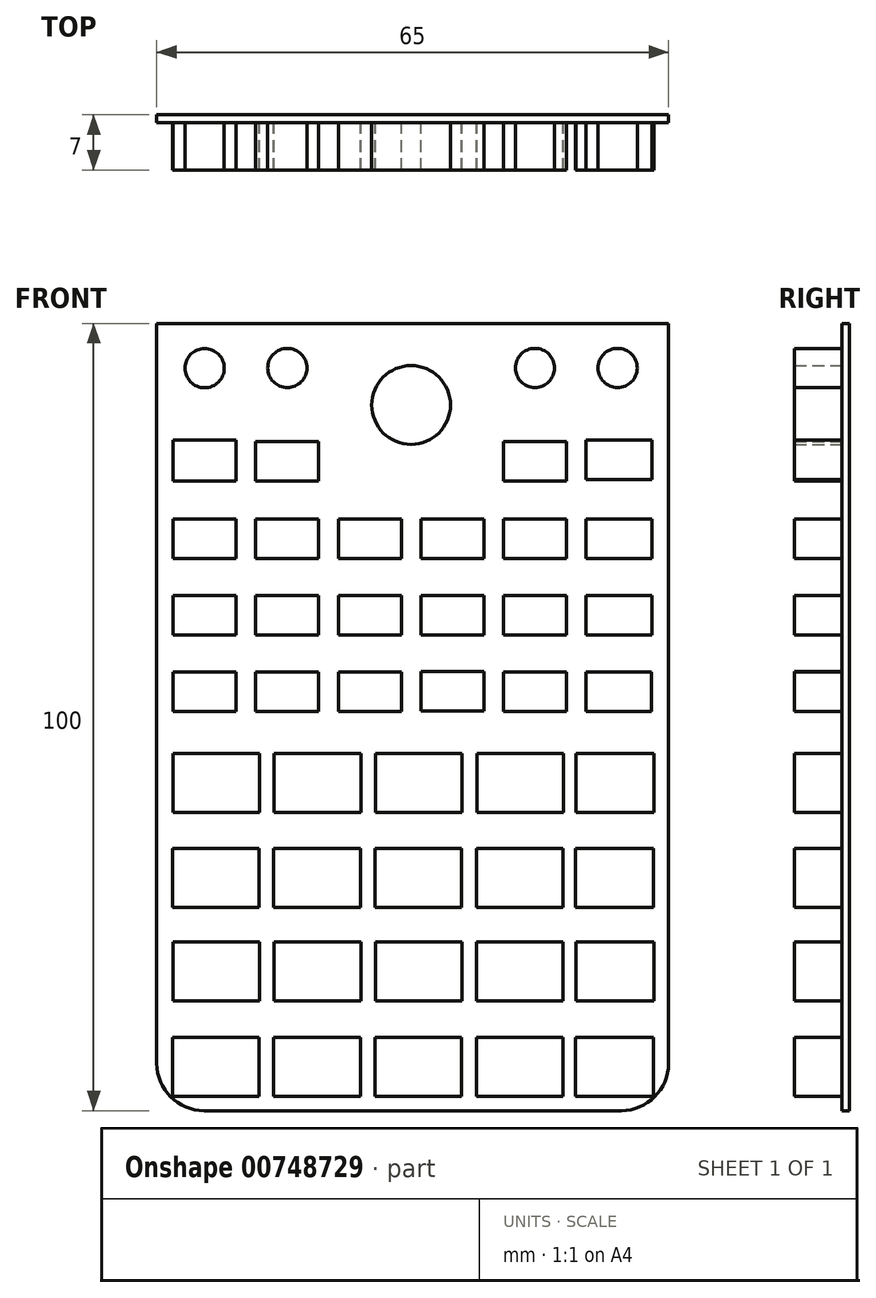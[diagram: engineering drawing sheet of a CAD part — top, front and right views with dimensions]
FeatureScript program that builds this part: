
annotation { "Feature Type Name" : "Feature", "Feature Type Description" : "" }
export const myFeature = defineFeature(function(context is Context, id is Id, definition is map)
    precondition{}
    {
        {
            var Q0;
            Q0=qCreatedBy(makeId("Front.planeOp"),FACE);
            var sketch = newSketch(context, id + "F0", { "sketchPlane" : qUnion([Q0])});
            skLineSegment(sketch, "E0.bottom", {"start": v(-31.37, 29.86) * mm, "end": v(33.63, 29.86) * mm});
            skLineSegment(sketch, "E0.top", {"start": v(-25.38, -70.14) * mm, "end": v(27.63, -70.14) * mm});
            skLineSegment(sketch, "E0.left", {"start": v(-31.37, 29.86) * mm, "end": v(-31.37, -64.14) * mm});
            skLineSegment(sketch, "E0.right", {"start": v(33.63, 29.86) * mm, "end": v(33.63, -64.14) * mm});
            skPoint(sketch, "E1.visualSharp", {"position": v(33.63, -70.14) * mm});
            skArc(sketch, "E1.filletArc", {"start": v(27.63, -70.14) * mm, "mid": v(31.87, -68.38) * mm, "end": v(33.63, -64.14) * mm});
            skPoint(sketch, "E2.visualSharp", {"position": v(-31.37, -70.14) * mm});
            skArc(sketch, "E2.filletArc", {"start": v(-31.37, -64.14) * mm, "mid": v(-29.62, -68.38) * mm, "end": v(-25.38, -70.14) * mm});
            skLineSegment(sketch, "E3", {"start": v(-29.36, -68.3) * mm, "end": v(-18.36, -68.3) * mm});
            skLineSegment(sketch, "E4", {"start": v(-18.36, -68.3) * mm, "end": v(-18.36, -60.81) * mm});
            skLineSegment(sketch, "E5", {"start": v(-18.36, -60.81) * mm, "end": v(-29.36, -60.81) * mm});
            skLineSegment(sketch, "E6", {"start": v(-29.36, -60.81) * mm, "end": v(-29.36, -68.3) * mm});
            skLineSegment(sketch, "E7", {"start": v(-29.36, -68.3) * mm, "end": v(-23.86, -68.3) * mm});
            skLineSegment(sketch, "E8", {"start": v(-16.51, -68.3) * mm, "end": v(-5.52, -68.3) * mm});
            skLineSegment(sketch, "E9", {"start": v(-5.52, -68.3) * mm, "end": v(-5.52, -60.81) * mm});
            skLineSegment(sketch, "E10", {"start": v(-5.52, -60.81) * mm, "end": v(-16.51, -60.81) * mm});
            skLineSegment(sketch, "E11", {"start": v(-16.51, -60.81) * mm, "end": v(-16.51, -68.3) * mm});
            skLineSegment(sketch, "E12", {"start": v(-16.51, -68.3) * mm, "end": v(-11.01, -68.3) * mm});
            skLineSegment(sketch, "E13", {"start": v(-3.66, -68.3) * mm, "end": v(7.34, -68.3) * mm});
            skLineSegment(sketch, "E14", {"start": v(7.34, -68.3) * mm, "end": v(7.34, -60.81) * mm});
            skLineSegment(sketch, "E15", {"start": v(7.34, -60.81) * mm, "end": v(-3.66, -60.81) * mm});
            skLineSegment(sketch, "E16", {"start": v(-3.66, -60.81) * mm, "end": v(-3.66, -68.3) * mm});
            skLineSegment(sketch, "E17", {"start": v(-3.66, -68.3) * mm, "end": v(1.84, -68.3) * mm});
            skLineSegment(sketch, "E18", {"start": v(9.22, -68.3) * mm, "end": v(20.22, -68.3) * mm});
            skLineSegment(sketch, "E19", {"start": v(20.22, -68.3) * mm, "end": v(20.22, -60.81) * mm});
            skLineSegment(sketch, "E20", {"start": v(20.22, -60.81) * mm, "end": v(9.22, -60.81) * mm});
            skLineSegment(sketch, "E21", {"start": v(9.22, -60.81) * mm, "end": v(9.22, -68.3) * mm});
            skLineSegment(sketch, "E22", {"start": v(9.22, -68.3) * mm, "end": v(14.72, -68.3) * mm});
            skLineSegment(sketch, "E23", {"start": v(21.82, -68.3) * mm, "end": v(31.72, -68.3) * mm});
            skLineSegment(sketch, "E24", {"start": v(31.72, -68.3) * mm, "end": v(31.72, -60.81) * mm});
            skLineSegment(sketch, "E25", {"start": v(31.72, -60.81) * mm, "end": v(21.82, -60.81) * mm});
            skLineSegment(sketch, "E26", {"start": v(21.82, -60.81) * mm, "end": v(21.82, -68.3) * mm});
            skLineSegment(sketch, "E27", {"start": v(21.82, -68.3) * mm, "end": v(26.49, -68.3) * mm});
            skLineSegment(sketch, "E28", {"start": v(-29.3, -56.22) * mm, "end": v(-18.3, -56.22) * mm});
            skLineSegment(sketch, "E29", {"start": v(-18.3, -56.22) * mm, "end": v(-18.3, -48.73) * mm});
            skLineSegment(sketch, "E30", {"start": v(-18.3, -48.73) * mm, "end": v(-29.3, -48.73) * mm});
            skLineSegment(sketch, "E31", {"start": v(-29.3, -48.73) * mm, "end": v(-29.3, -56.22) * mm});
            skLineSegment(sketch, "E32", {"start": v(-29.3, -56.22) * mm, "end": v(-23.8, -56.22) * mm});
            skLineSegment(sketch, "E33", {"start": v(-16.45, -56.22) * mm, "end": v(-5.45, -56.22) * mm});
            skLineSegment(sketch, "E34", {"start": v(-5.45, -56.22) * mm, "end": v(-5.45, -48.73) * mm});
            skLineSegment(sketch, "E35", {"start": v(-5.45, -48.73) * mm, "end": v(-16.45, -48.73) * mm});
            skLineSegment(sketch, "E36", {"start": v(-16.45, -48.73) * mm, "end": v(-16.45, -56.22) * mm});
            skLineSegment(sketch, "E37", {"start": v(-16.45, -56.22) * mm, "end": v(-10.95, -56.22) * mm});
            skLineSegment(sketch, "E38", {"start": v(-3.6, -56.22) * mm, "end": v(7.4, -56.22) * mm});
            skLineSegment(sketch, "E39", {"start": v(7.4, -56.22) * mm, "end": v(7.4, -48.73) * mm});
            skLineSegment(sketch, "E40", {"start": v(7.4, -48.73) * mm, "end": v(-3.6, -48.73) * mm});
            skLineSegment(sketch, "E41", {"start": v(-3.6, -48.73) * mm, "end": v(-3.6, -56.22) * mm});
            skLineSegment(sketch, "E42", {"start": v(-3.6, -56.22) * mm, "end": v(1.9, -56.22) * mm});
            skLineSegment(sketch, "E43", {"start": v(21.88, -56.22) * mm, "end": v(31.78, -56.22) * mm});
            skLineSegment(sketch, "E44", {"start": v(31.78, -56.22) * mm, "end": v(31.78, -48.73) * mm});
            skLineSegment(sketch, "E45", {"start": v(31.78, -48.73) * mm, "end": v(21.88, -48.73) * mm});
            skLineSegment(sketch, "E46", {"start": v(21.88, -48.73) * mm, "end": v(21.88, -56.22) * mm});
            skLineSegment(sketch, "E47", {"start": v(21.88, -56.22) * mm, "end": v(26.55, -56.22) * mm});
            skPoint(sketch, "E48.visualSharp", {"position": v(-31.37, -46.14) * mm});
            skLineSegment(sketch, "E49", {"start": v(-29.36, -44.3) * mm, "end": v(-18.36, -44.3) * mm});
            skLineSegment(sketch, "E50", {"start": v(-18.36, -44.3) * mm, "end": v(-18.36, -36.81) * mm});
            skLineSegment(sketch, "E51", {"start": v(-18.36, -36.81) * mm, "end": v(-29.36, -36.81) * mm});
            skLineSegment(sketch, "E52", {"start": v(-29.36, -36.81) * mm, "end": v(-29.36, -44.3) * mm});
            skLineSegment(sketch, "E53", {"start": v(-29.36, -44.3) * mm, "end": v(-23.86, -44.3) * mm});
            skLineSegment(sketch, "E54", {"start": v(-16.51, -44.3) * mm, "end": v(-5.52, -44.3) * mm});
            skLineSegment(sketch, "E55", {"start": v(-5.52, -44.3) * mm, "end": v(-5.52, -36.81) * mm});
            skLineSegment(sketch, "E56", {"start": v(-5.52, -36.81) * mm, "end": v(-16.51, -36.81) * mm});
            skLineSegment(sketch, "E57", {"start": v(-16.51, -36.81) * mm, "end": v(-16.51, -44.3) * mm});
            skLineSegment(sketch, "E58", {"start": v(-16.51, -44.3) * mm, "end": v(-11.01, -44.3) * mm});
            skLineSegment(sketch, "E59", {"start": v(-3.66, -44.3) * mm, "end": v(7.34, -44.3) * mm});
            skLineSegment(sketch, "E60", {"start": v(7.34, -44.3) * mm, "end": v(7.34, -36.81) * mm});
            skLineSegment(sketch, "E61", {"start": v(7.34, -36.81) * mm, "end": v(-3.66, -36.81) * mm});
            skLineSegment(sketch, "E62", {"start": v(-3.66, -36.81) * mm, "end": v(-3.66, -44.3) * mm});
            skLineSegment(sketch, "E63", {"start": v(-3.66, -44.3) * mm, "end": v(1.84, -44.3) * mm});
            skLineSegment(sketch, "E64", {"start": v(9.22, -44.3) * mm, "end": v(20.22, -44.3) * mm});
            skLineSegment(sketch, "E65", {"start": v(20.22, -44.3) * mm, "end": v(20.22, -36.81) * mm});
            skLineSegment(sketch, "E66", {"start": v(20.22, -36.81) * mm, "end": v(9.22, -36.81) * mm});
            skLineSegment(sketch, "E67", {"start": v(9.22, -36.81) * mm, "end": v(9.22, -44.3) * mm});
            skLineSegment(sketch, "E68", {"start": v(9.22, -44.3) * mm, "end": v(14.72, -44.3) * mm});
            skLineSegment(sketch, "E69", {"start": v(21.82, -44.3) * mm, "end": v(31.72, -44.3) * mm});
            skLineSegment(sketch, "E70", {"start": v(31.72, -44.3) * mm, "end": v(31.72, -36.81) * mm});
            skLineSegment(sketch, "E71", {"start": v(31.72, -36.81) * mm, "end": v(21.82, -36.81) * mm});
            skLineSegment(sketch, "E72", {"start": v(21.82, -36.81) * mm, "end": v(21.82, -44.3) * mm});
            skLineSegment(sketch, "E73", {"start": v(21.82, -44.3) * mm, "end": v(26.49, -44.3) * mm});
            skLineSegment(sketch, "E74", {"start": v(-29.3, -32.22) * mm, "end": v(-18.3, -32.22) * mm});
            skLineSegment(sketch, "E75", {"start": v(-18.3, -32.22) * mm, "end": v(-18.3, -24.73) * mm});
            skLineSegment(sketch, "E76", {"start": v(-18.3, -24.73) * mm, "end": v(-29.3, -24.73) * mm});
            skLineSegment(sketch, "E77", {"start": v(-29.3, -24.73) * mm, "end": v(-29.3, -32.22) * mm});
            skLineSegment(sketch, "E78", {"start": v(-29.3, -32.22) * mm, "end": v(-23.8, -32.22) * mm});
            skLineSegment(sketch, "E79", {"start": v(-16.45, -32.22) * mm, "end": v(-5.45, -32.22) * mm});
            skLineSegment(sketch, "E80", {"start": v(-5.45, -32.22) * mm, "end": v(-5.45, -24.73) * mm});
            skLineSegment(sketch, "E81", {"start": v(-5.45, -24.73) * mm, "end": v(-16.45, -24.73) * mm});
            skLineSegment(sketch, "E82", {"start": v(-16.45, -24.73) * mm, "end": v(-16.45, -32.22) * mm});
            skLineSegment(sketch, "E83", {"start": v(-16.45, -32.22) * mm, "end": v(-10.95, -32.22) * mm});
            skLineSegment(sketch, "E84", {"start": v(-3.6, -32.22) * mm, "end": v(7.4, -32.22) * mm});
            skLineSegment(sketch, "E85", {"start": v(7.4, -32.22) * mm, "end": v(7.4, -24.73) * mm});
            skLineSegment(sketch, "E86", {"start": v(7.4, -24.73) * mm, "end": v(-3.6, -24.73) * mm});
            skLineSegment(sketch, "E87", {"start": v(-3.6, -24.73) * mm, "end": v(-3.6, -32.22) * mm});
            skLineSegment(sketch, "E88", {"start": v(-3.6, -32.22) * mm, "end": v(1.9, -32.22) * mm});
            skLineSegment(sketch, "E89", {"start": v(9.28, -32.22) * mm, "end": v(20.28, -32.22) * mm});
            skLineSegment(sketch, "E90", {"start": v(20.28, -32.22) * mm, "end": v(20.28, -24.73) * mm});
            skLineSegment(sketch, "E91", {"start": v(20.28, -24.73) * mm, "end": v(9.28, -24.73) * mm});
            skLineSegment(sketch, "E92", {"start": v(9.28, -24.73) * mm, "end": v(9.28, -32.22) * mm});
            skLineSegment(sketch, "E93", {"start": v(9.28, -32.22) * mm, "end": v(14.78, -32.22) * mm});
            skLineSegment(sketch, "E94", {"start": v(21.88, -32.22) * mm, "end": v(31.78, -32.22) * mm});
            skLineSegment(sketch, "E95", {"start": v(31.78, -32.22) * mm, "end": v(31.78, -24.73) * mm});
            skLineSegment(sketch, "E96", {"start": v(31.78, -24.73) * mm, "end": v(21.88, -24.73) * mm});
            skLineSegment(sketch, "E97", {"start": v(21.88, -24.73) * mm, "end": v(21.88, -32.22) * mm});
            skLineSegment(sketch, "E98", {"start": v(21.88, -32.22) * mm, "end": v(26.55, -32.22) * mm});
            skLineSegment(sketch, "E99", {"start": v(-29.3, -19.4) * mm, "end": v(-21.3, -19.4) * mm});
            skLineSegment(sketch, "E100", {"start": v(-21.3, -19.4) * mm, "end": v(-21.3, -14.4) * mm});
            skLineSegment(sketch, "E101", {"start": v(-21.3, -14.4) * mm, "end": v(-29.3, -14.4) * mm});
            skLineSegment(sketch, "E102", {"start": v(-29.3, -14.4) * mm, "end": v(-29.3, -19.4) * mm});
            skLineSegment(sketch, "E103", {"start": v(-29.3, -19.4) * mm, "end": v(-26.94, -19.4) * mm});
            skLineSegment(sketch, "E104", {"start": v(-18.8, -19.4) * mm, "end": v(-10.8, -19.4) * mm});
            skLineSegment(sketch, "E105", {"start": v(-10.8, -19.4) * mm, "end": v(-10.8, -14.4) * mm});
            skLineSegment(sketch, "E106", {"start": v(-10.8, -14.4) * mm, "end": v(-18.8, -14.4) * mm});
            skLineSegment(sketch, "E107", {"start": v(-18.8, -14.4) * mm, "end": v(-18.8, -19.4) * mm});
            skLineSegment(sketch, "E108", {"start": v(-18.8, -19.4) * mm, "end": v(-16.45, -19.4) * mm});
            skLineSegment(sketch, "E109", {"start": v(-8.31, -19.4) * mm, "end": v(-0.31, -19.4) * mm});
            skLineSegment(sketch, "E110", {"start": v(-0.31, -19.4) * mm, "end": v(-0.31, -14.38) * mm});
            skLineSegment(sketch, "E111", {"start": v(-0.31, -14.38) * mm, "end": v(-8.31, -14.38) * mm});
            skLineSegment(sketch, "E112", {"start": v(-8.31, -14.38) * mm, "end": v(-8.31, -19.4) * mm});
            skLineSegment(sketch, "E113", {"start": v(-8.31, -19.4) * mm, "end": v(-6.48, -19.4) * mm});
            skLineSegment(sketch, "E114", {"start": v(2.18, -19.38) * mm, "end": v(10.18, -19.38) * mm});
            skLineSegment(sketch, "E115", {"start": v(10.18, -19.38) * mm, "end": v(10.18, -14.38) * mm});
            skLineSegment(sketch, "E116", {"start": v(10.18, -14.38) * mm, "end": v(2.18, -14.38) * mm});
            skLineSegment(sketch, "E117", {"start": v(2.18, -14.38) * mm, "end": v(2.18, -19.38) * mm});
            skLineSegment(sketch, "E118", {"start": v(12.67, -19.4) * mm, "end": v(20.67, -19.4) * mm});
            skLineSegment(sketch, "E119", {"start": v(20.67, -19.4) * mm, "end": v(20.67, -14.41) * mm});
            skLineSegment(sketch, "E120", {"start": v(20.67, -14.41) * mm, "end": v(12.67, -14.41) * mm});
            skLineSegment(sketch, "E121", {"start": v(12.67, -14.41) * mm, "end": v(12.67, -19.4) * mm});
            skLineSegment(sketch, "E122", {"start": v(12.67, -19.4) * mm, "end": v(13.52, -19.4) * mm});
            skLineSegment(sketch, "E123", {"start": v(23.16, -19.42) * mm, "end": v(31.5, -19.42) * mm});
            skLineSegment(sketch, "E124", {"start": v(31.5, -19.42) * mm, "end": v(31.5, -14.41) * mm});
            skLineSegment(sketch, "E125", {"start": v(31.5, -14.41) * mm, "end": v(23.16, -14.41) * mm});
            skLineSegment(sketch, "E126", {"start": v(23.16, -14.41) * mm, "end": v(23.16, -19.42) * mm});
            skLineSegment(sketch, "E127", {"start": v(23.16, -19.42) * mm, "end": v(25.5, -19.42) * mm});
            skLineSegment(sketch, "E128", {"start": v(-29.3, -9.7) * mm, "end": v(-21.3, -9.7) * mm});
            skLineSegment(sketch, "E129", {"start": v(-21.3, -9.7) * mm, "end": v(-21.3, -4.7) * mm});
            skLineSegment(sketch, "E130", {"start": v(-21.3, -4.7) * mm, "end": v(-29.3, -4.7) * mm});
            skLineSegment(sketch, "E131", {"start": v(-29.3, -4.7) * mm, "end": v(-29.3, -9.7) * mm});
            skLineSegment(sketch, "E132", {"start": v(-29.3, -9.7) * mm, "end": v(-25.28, -9.7) * mm});
            skLineSegment(sketch, "E133", {"start": v(-18.8, -9.7) * mm, "end": v(-10.8, -9.7) * mm});
            skLineSegment(sketch, "E134", {"start": v(-10.8, -9.7) * mm, "end": v(-10.8, -4.7) * mm});
            skLineSegment(sketch, "E135", {"start": v(-10.8, -4.7) * mm, "end": v(-18.8, -4.7) * mm});
            skLineSegment(sketch, "E136", {"start": v(-18.8, -4.7) * mm, "end": v(-18.8, -9.7) * mm});
            skLineSegment(sketch, "E137", {"start": v(-18.8, -9.7) * mm, "end": v(-14.8, -9.7) * mm});
            skLineSegment(sketch, "E138", {"start": v(-8.31, -9.7) * mm, "end": v(-0.31, -9.7) * mm});
            skLineSegment(sketch, "E139", {"start": v(-0.31, -9.7) * mm, "end": v(-0.31, -4.7) * mm});
            skLineSegment(sketch, "E140", {"start": v(-0.31, -4.7) * mm, "end": v(-8.31, -4.7) * mm});
            skLineSegment(sketch, "E141", {"start": v(-8.31, -4.7) * mm, "end": v(-8.31, -9.7) * mm});
            skLineSegment(sketch, "E142", {"start": v(-8.31, -9.7) * mm, "end": v(-4.82, -9.7) * mm});
            skLineSegment(sketch, "E143", {"start": v(2.18, -9.7) * mm, "end": v(10.18, -9.7) * mm});
            skLineSegment(sketch, "E144", {"start": v(10.18, -9.7) * mm, "end": v(10.18, -4.7) * mm});
            skLineSegment(sketch, "E145", {"start": v(10.18, -4.7) * mm, "end": v(2.18, -4.7) * mm});
            skLineSegment(sketch, "E146", {"start": v(2.18, -4.7) * mm, "end": v(2.18, -9.7) * mm});
            skLineSegment(sketch, "E147", {"start": v(12.67, -9.7) * mm, "end": v(20.67, -9.7) * mm});
            skLineSegment(sketch, "E148", {"start": v(20.67, -9.7) * mm, "end": v(20.67, -4.7) * mm});
            skLineSegment(sketch, "E149", {"start": v(20.67, -4.7) * mm, "end": v(12.67, -4.7) * mm});
            skLineSegment(sketch, "E150", {"start": v(12.67, -4.7) * mm, "end": v(12.67, -9.7) * mm});
            skLineSegment(sketch, "E151", {"start": v(12.67, -9.7) * mm, "end": v(15.18, -9.7) * mm});
            skLineSegment(sketch, "E152", {"start": v(23.16, -9.7) * mm, "end": v(31.5, -9.7) * mm});
            skLineSegment(sketch, "E153", {"start": v(31.5, -9.7) * mm, "end": v(31.5, -4.7) * mm});
            skLineSegment(sketch, "E154", {"start": v(31.5, -4.7) * mm, "end": v(23.16, -4.7) * mm});
            skLineSegment(sketch, "E155", {"start": v(23.16, -4.7) * mm, "end": v(23.16, -9.7) * mm});
            skLineSegment(sketch, "E156", {"start": v(23.16, -9.7) * mm, "end": v(27.17, -9.7) * mm});
            skLineSegment(sketch, "E157", {"start": v(-29.3, 0) * mm, "end": v(-21.3, 0) * mm});
            skLineSegment(sketch, "E158", {"start": v(-21.3, 0) * mm, "end": v(-21.3, 5) * mm});
            skLineSegment(sketch, "E159", {"start": v(-21.3, 5) * mm, "end": v(-29.3, 5) * mm});
            skLineSegment(sketch, "E160", {"start": v(-29.3, 5) * mm, "end": v(-29.3, 0) * mm});
            skLineSegment(sketch, "E161", {"start": v(-29.3, 0) * mm, "end": v(-25.28, 0) * mm});
            skLineSegment(sketch, "E162", {"start": v(-18.8, 0) * mm, "end": v(-10.8, 0) * mm});
            skLineSegment(sketch, "E163", {"start": v(-10.8, 0) * mm, "end": v(-10.8, 5) * mm});
            skLineSegment(sketch, "E164", {"start": v(-10.8, 5) * mm, "end": v(-18.8, 5) * mm});
            skLineSegment(sketch, "E165", {"start": v(-18.8, 5) * mm, "end": v(-18.8, 0) * mm});
            skLineSegment(sketch, "E166", {"start": v(-18.8, 0) * mm, "end": v(-14.8, 0) * mm});
            skLineSegment(sketch, "E167", {"start": v(-8.31, 0) * mm, "end": v(-0.31, 0) * mm});
            skLineSegment(sketch, "E168", {"start": v(-0.31, 0) * mm, "end": v(-0.31, 5) * mm});
            skLineSegment(sketch, "E169", {"start": v(-0.31, 5) * mm, "end": v(-8.31, 5) * mm});
            skLineSegment(sketch, "E170", {"start": v(-8.31, 5) * mm, "end": v(-8.31, 0) * mm});
            skLineSegment(sketch, "E171", {"start": v(-8.31, 0) * mm, "end": v(-4.82, 0) * mm});
            skLineSegment(sketch, "E172", {"start": v(2.18, 0) * mm, "end": v(10.18, 0) * mm});
            skLineSegment(sketch, "E173", {"start": v(10.18, 0) * mm, "end": v(10.18, 5) * mm});
            skLineSegment(sketch, "E174", {"start": v(10.18, 5) * mm, "end": v(2.18, 5) * mm});
            skLineSegment(sketch, "E175", {"start": v(2.18, 5) * mm, "end": v(2.18, 0) * mm});
            skLineSegment(sketch, "E176", {"start": v(12.67, 0) * mm, "end": v(20.67, 0) * mm});
            skLineSegment(sketch, "E177", {"start": v(20.67, 0) * mm, "end": v(20.67, 5) * mm});
            skLineSegment(sketch, "E178", {"start": v(20.67, 5) * mm, "end": v(12.67, 5) * mm});
            skLineSegment(sketch, "E179", {"start": v(12.67, 5) * mm, "end": v(12.67, 0) * mm});
            skLineSegment(sketch, "E180", {"start": v(12.67, 0) * mm, "end": v(15.18, 0) * mm});
            skLineSegment(sketch, "E181", {"start": v(23.16, 0) * mm, "end": v(31.5, 0) * mm});
            skLineSegment(sketch, "E182", {"start": v(31.5, 0) * mm, "end": v(31.5, 5) * mm});
            skLineSegment(sketch, "E183", {"start": v(31.5, 5) * mm, "end": v(23.16, 5) * mm});
            skLineSegment(sketch, "E184", {"start": v(23.16, 5) * mm, "end": v(23.16, 0) * mm});
            skLineSegment(sketch, "E185", {"start": v(23.16, 0) * mm, "end": v(27.17, 0) * mm});
            skLineSegment(sketch, "E186", {"start": v(-29.3, 9.86) * mm, "end": v(-21.3, 9.86) * mm});
            skLineSegment(sketch, "E187", {"start": v(-21.3, 9.86) * mm, "end": v(-21.3, 15.03) * mm});
            skLineSegment(sketch, "E188", {"start": v(-21.3, 15.03) * mm, "end": v(-29.3, 15.03) * mm});
            skLineSegment(sketch, "E189", {"start": v(-29.3, 15.03) * mm, "end": v(-29.3, 9.86) * mm});
            skLineSegment(sketch, "E190", {"start": v(-29.3, 9.86) * mm, "end": v(-25.28, 9.86) * mm});
            skLineSegment(sketch, "E191", {"start": v(-18.8, 9.86) * mm, "end": v(-10.8, 9.86) * mm});
            skLineSegment(sketch, "E192", {"start": v(-10.8, 9.86) * mm, "end": v(-10.8, 14.86) * mm});
            skLineSegment(sketch, "E193", {"start": v(-10.8, 14.86) * mm, "end": v(-18.8, 14.86) * mm});
            skLineSegment(sketch, "E194", {"start": v(-18.8, 14.86) * mm, "end": v(-18.8, 9.86) * mm});
            skLineSegment(sketch, "E195", {"start": v(-18.8, 9.86) * mm, "end": v(-14.8, 9.86) * mm});
            skLineSegment(sketch, "E196", {"start": v(12.67, 9.86) * mm, "end": v(20.67, 9.86) * mm});
            skLineSegment(sketch, "E197", {"start": v(20.67, 9.86) * mm, "end": v(20.67, 14.86) * mm});
            skLineSegment(sketch, "E198", {"start": v(20.67, 14.86) * mm, "end": v(12.67, 14.86) * mm});
            skLineSegment(sketch, "E199", {"start": v(12.67, 14.86) * mm, "end": v(12.67, 9.86) * mm});
            skLineSegment(sketch, "E200", {"start": v(12.67, 9.86) * mm, "end": v(15.18, 9.86) * mm});
            skLineSegment(sketch, "E201", {"start": v(23.16, 10.03) * mm, "end": v(31.5, 10.03) * mm});
            skLineSegment(sketch, "E202", {"start": v(31.5, 10.03) * mm, "end": v(31.5, 15.03) * mm});
            skLineSegment(sketch, "E203", {"start": v(31.5, 15.03) * mm, "end": v(23.16, 15.03) * mm});
            skLineSegment(sketch, "E204", {"start": v(23.16, 15.03) * mm, "end": v(23.16, 10.03) * mm});
            skLineSegment(sketch, "E205", {"start": v(23.16, 10.03) * mm, "end": v(27.17, 10.03) * mm});
            skLineSegment(sketch, "E206", {"start": v(10.18, 0) * mm, "end": v(10.18, 2.51) * mm});
            skCircle(sketch, "E207", {"center": v(-14.8, 24.21) * mm, "radius": 2.49 * mm});
            skCircle(sketch, "E208", {"center": v(0.93, 19.5) * mm, "radius": 5 * mm});
            skLineSegment(sketch, "E209", {"start": v(12.67, 9.86) * mm, "end": v(16.67, 9.86) * mm});
            skCircle(sketch, "E210", {"center": v(16.67, 24.21) * mm, "radius": 2.49 * mm});
            skCircle(sketch, "E211", {"center": v(27.17, 24.21) * mm, "radius": 2.49 * mm});
            skCircle(sketch, "E212", {"center": v(-25.3, 24.19) * mm, "radius": 2.49 * mm});
            skLineSegment(sketch, "E213", {"start": v(-3.6, -48.73) * mm, "end": v(7.4, -48.73) * mm});
            skLineSegment(sketch, "E214", {"start": v(9.22, -48.73) * mm, "end": v(9.22, -56.22) * mm});
            skLineSegment(sketch, "E215", {"start": v(9.22, -56.22) * mm, "end": v(20.22, -56.22) * mm});
            skLineSegment(sketch, "E216", {"start": v(20.22, -56.22) * mm, "end": v(20.22, -48.73) * mm});
            skLineSegment(sketch, "E217", {"start": v(20.22, -48.73) * mm, "end": v(9.22, -48.73) * mm});
            skSolve(sketch);
        }
        {
            var Q0;
            Q0=makeQuery(id+"F0.imprint","IMPRINT",FACE,{"disambiguationData":[TD([[makeQuery(id+"F0.imprint","IMPRINT",EDGE,{"derivedFrom":sQuery(id+"F0.wireOp",EDGE,"E0.bottom")}),-1.0]])]});
            extrude(context, id + "F1", {"entities" : qUnion([Q0]), "depth" : 1 * mm, "offsetDistance" : 25.4 * mm});
        }
        {
            var Q0;
            Q0=makeQuery(id+"F0.imprint","IMPRINT",FACE,{"disambiguationData":[TD([[makeQuery(id+"F0.imprint","IMPRINT",EDGE,{"derivedFrom":sQuery(id+"F0.wireOp",EDGE,"E3")}),1.0]])]});
            var Q1;
            Q1=makeQuery(id+"F0.imprint","IMPRINT",FACE,{"disambiguationData":[TD([[makeQuery(id+"F0.imprint","IMPRINT",EDGE,{"derivedFrom":sQuery(id+"F0.wireOp",EDGE,"E8")}),1.0]])]});
            var Q2;
            Q2=makeQuery(id+"F0.imprint","IMPRINT",FACE,{"disambiguationData":[TD([[makeQuery(id+"F0.imprint","IMPRINT",EDGE,{"derivedFrom":sQuery(id+"F0.wireOp",EDGE,"E13")}),1.0]])]});
            var Q3;
            Q3=makeQuery(id+"F0.imprint","IMPRINT",FACE,{"disambiguationData":[TD([[makeQuery(id+"F0.imprint","IMPRINT",EDGE,{"derivedFrom":sQuery(id+"F0.wireOp",EDGE,"E18")}),1.0]])]});
            var Q4;
            Q4=makeQuery(id+"F0.imprint","IMPRINT",FACE,{"disambiguationData":[TD([[makeQuery(id+"F0.imprint","IMPRINT",EDGE,{"derivedFrom":sQuery(id+"F0.wireOp",EDGE,"E23")}),1.0]])]});
            var Q5;
            Q5=makeQuery(id+"F0.imprint","IMPRINT",FACE,{"disambiguationData":[TD([[makeQuery(id+"F0.imprint","IMPRINT",EDGE,{"derivedFrom":sQuery(id+"F0.wireOp",EDGE,"E43")}),1.0]])]});
            var Q6;
            Q6=makeQuery(id+"F0.imprint","IMPRINT",FACE,{"disambiguationData":[TD([[makeQuery(id+"F0.imprint","IMPRINT",EDGE,{"derivedFrom":sQuery(id+"F0.wireOp",EDGE,"E214")}),1.0]])]});
            var Q7;
            {var subQ3=sQuery(id+"F0.wireOp",EDGE,"E39");Q7=makeQuery(id+"F0.imprint","IMPRINT",FACE,{"disambiguationData":[TD([[makeQuery(id+"F0.imprint","IMPRINT",EDGE,{"derivedFrom":subQ3}),1.0]])]});}
            var Q8;
            Q8=makeQuery(id+"F0.imprint","IMPRINT",FACE,{"disambiguationData":[TD([[makeQuery(id+"F0.imprint","IMPRINT",EDGE,{"derivedFrom":sQuery(id+"F0.wireOp",EDGE,"E33")}),1.0]])]});
            var Q9;
            Q9=makeQuery(id+"F0.imprint","IMPRINT",FACE,{"disambiguationData":[TD([[makeQuery(id+"F0.imprint","IMPRINT",EDGE,{"derivedFrom":sQuery(id+"F0.wireOp",EDGE,"E28")}),1.0]])]});
            var Q10;
            Q10=makeQuery(id+"F0.imprint","IMPRINT",FACE,{"disambiguationData":[TD([[makeQuery(id+"F0.imprint","IMPRINT",EDGE,{"derivedFrom":sQuery(id+"F0.wireOp",EDGE,"E49")}),1.0]])]});
            var Q11;
            Q11=makeQuery(id+"F0.imprint","IMPRINT",FACE,{"disambiguationData":[TD([[makeQuery(id+"F0.imprint","IMPRINT",EDGE,{"derivedFrom":sQuery(id+"F0.wireOp",EDGE,"E54")}),1.0]])]});
            var Q12;
            Q12=makeQuery(id+"F0.imprint","IMPRINT",FACE,{"disambiguationData":[TD([[makeQuery(id+"F0.imprint","IMPRINT",EDGE,{"derivedFrom":sQuery(id+"F0.wireOp",EDGE,"E59")}),1.0]])]});
            var Q13;
            Q13=makeQuery(id+"F0.imprint","IMPRINT",FACE,{"disambiguationData":[TD([[makeQuery(id+"F0.imprint","IMPRINT",EDGE,{"derivedFrom":sQuery(id+"F0.wireOp",EDGE,"E64")}),1.0]])]});
            var Q14;
            Q14=makeQuery(id+"F0.imprint","IMPRINT",FACE,{"disambiguationData":[TD([[makeQuery(id+"F0.imprint","IMPRINT",EDGE,{"derivedFrom":sQuery(id+"F0.wireOp",EDGE,"E69")}),1.0]])]});
            var Q15;
            Q15=makeQuery(id+"F0.imprint","IMPRINT",FACE,{"disambiguationData":[TD([[makeQuery(id+"F0.imprint","IMPRINT",EDGE,{"derivedFrom":sQuery(id+"F0.wireOp",EDGE,"E94")}),1.0]])]});
            var Q16;
            Q16=makeQuery(id+"F0.imprint","IMPRINT",FACE,{"disambiguationData":[TD([[makeQuery(id+"F0.imprint","IMPRINT",EDGE,{"derivedFrom":sQuery(id+"F0.wireOp",EDGE,"E89")}),1.0]])]});
            var Q17;
            Q17=makeQuery(id+"F0.imprint","IMPRINT",FACE,{"disambiguationData":[TD([[makeQuery(id+"F0.imprint","IMPRINT",EDGE,{"derivedFrom":sQuery(id+"F0.wireOp",EDGE,"E84")}),1.0]])]});
            var Q18;
            Q18=makeQuery(id+"F0.imprint","IMPRINT",FACE,{"disambiguationData":[TD([[makeQuery(id+"F0.imprint","IMPRINT",EDGE,{"derivedFrom":sQuery(id+"F0.wireOp",EDGE,"E79")}),1.0]])]});
            var Q19;
            Q19=makeQuery(id+"F0.imprint","IMPRINT",FACE,{"disambiguationData":[TD([[makeQuery(id+"F0.imprint","IMPRINT",EDGE,{"derivedFrom":sQuery(id+"F0.wireOp",EDGE,"E74")}),1.0]])]});
            var Q20;
            Q20=makeQuery(id+"F0.imprint","IMPRINT",FACE,{"disambiguationData":[TD([[makeQuery(id+"F0.imprint","IMPRINT",EDGE,{"derivedFrom":sQuery(id+"F0.wireOp",EDGE,"E99")}),1.0]])]});
            var Q21;
            Q21=makeQuery(id+"F0.imprint","IMPRINT",FACE,{"disambiguationData":[TD([[makeQuery(id+"F0.imprint","IMPRINT",EDGE,{"derivedFrom":sQuery(id+"F0.wireOp",EDGE,"E104")}),1.0]])]});
            var Q22;
            Q22=makeQuery(id+"F0.imprint","IMPRINT",FACE,{"disambiguationData":[TD([[makeQuery(id+"F0.imprint","IMPRINT",EDGE,{"derivedFrom":sQuery(id+"F0.wireOp",EDGE,"E109")}),1.0]])]});
            var Q23;
            Q23=makeQuery(id+"F0.imprint","IMPRINT",FACE,{"disambiguationData":[TD([[makeQuery(id+"F0.imprint","IMPRINT",EDGE,{"derivedFrom":sQuery(id+"F0.wireOp",EDGE,"E114")}),1.0]])]});
            var Q24;
            Q24=makeQuery(id+"F0.imprint","IMPRINT",FACE,{"disambiguationData":[TD([[makeQuery(id+"F0.imprint","IMPRINT",EDGE,{"derivedFrom":sQuery(id+"F0.wireOp",EDGE,"E118")}),1.0]])]});
            var Q25;
            Q25=makeQuery(id+"F0.imprint","IMPRINT",FACE,{"disambiguationData":[TD([[makeQuery(id+"F0.imprint","IMPRINT",EDGE,{"derivedFrom":sQuery(id+"F0.wireOp",EDGE,"E123")}),1.0]])]});
            var Q26;
            Q26=makeQuery(id+"F0.imprint","IMPRINT",FACE,{"disambiguationData":[TD([[makeQuery(id+"F0.imprint","IMPRINT",EDGE,{"derivedFrom":sQuery(id+"F0.wireOp",EDGE,"E152")}),1.0]])]});
            var Q27;
            Q27=makeQuery(id+"F0.imprint","IMPRINT",FACE,{"disambiguationData":[TD([[makeQuery(id+"F0.imprint","IMPRINT",EDGE,{"derivedFrom":sQuery(id+"F0.wireOp",EDGE,"E147")}),1.0]])]});
            var Q28;
            Q28=makeQuery(id+"F0.imprint","IMPRINT",FACE,{"disambiguationData":[TD([[makeQuery(id+"F0.imprint","IMPRINT",EDGE,{"derivedFrom":sQuery(id+"F0.wireOp",EDGE,"E143")}),1.0]])]});
            var Q29;
            Q29=makeQuery(id+"F0.imprint","IMPRINT",FACE,{"disambiguationData":[TD([[makeQuery(id+"F0.imprint","IMPRINT",EDGE,{"derivedFrom":sQuery(id+"F0.wireOp",EDGE,"E138")}),1.0]])]});
            var Q30;
            Q30=makeQuery(id+"F0.imprint","IMPRINT",FACE,{"disambiguationData":[TD([[makeQuery(id+"F0.imprint","IMPRINT",EDGE,{"derivedFrom":sQuery(id+"F0.wireOp",EDGE,"E133")}),1.0]])]});
            var Q31;
            Q31=makeQuery(id+"F0.imprint","IMPRINT",FACE,{"disambiguationData":[TD([[makeQuery(id+"F0.imprint","IMPRINT",EDGE,{"derivedFrom":sQuery(id+"F0.wireOp",EDGE,"E128")}),1.0]])]});
            var Q32;
            Q32=makeQuery(id+"F0.imprint","IMPRINT",FACE,{"disambiguationData":[TD([[makeQuery(id+"F0.imprint","IMPRINT",EDGE,{"derivedFrom":sQuery(id+"F0.wireOp",EDGE,"E157")}),1.0]])]});
            var Q33;
            Q33=makeQuery(id+"F0.imprint","IMPRINT",FACE,{"disambiguationData":[TD([[makeQuery(id+"F0.imprint","IMPRINT",EDGE,{"derivedFrom":sQuery(id+"F0.wireOp",EDGE,"E162")}),1.0]])]});
            var Q34;
            Q34=makeQuery(id+"F0.imprint","IMPRINT",FACE,{"disambiguationData":[TD([[makeQuery(id+"F0.imprint","IMPRINT",EDGE,{"derivedFrom":sQuery(id+"F0.wireOp",EDGE,"E167")}),1.0]])]});
            var Q35;
            Q35=makeQuery(id+"F0.imprint","IMPRINT",FACE,{"disambiguationData":[TD([[makeQuery(id+"F0.imprint","IMPRINT",EDGE,{"derivedFrom":sQuery(id+"F0.wireOp",EDGE,"E172")}),1.0]])]});
            var Q36;
            Q36=makeQuery(id+"F0.imprint","IMPRINT",FACE,{"disambiguationData":[TD([[makeQuery(id+"F0.imprint","IMPRINT",EDGE,{"derivedFrom":sQuery(id+"F0.wireOp",EDGE,"E176")}),1.0]])]});
            var Q37;
            Q37=makeQuery(id+"F0.imprint","IMPRINT",FACE,{"disambiguationData":[TD([[makeQuery(id+"F0.imprint","IMPRINT",EDGE,{"derivedFrom":sQuery(id+"F0.wireOp",EDGE,"E181")}),1.0]])]});
            var Q38;
            Q38=makeQuery(id+"F0.imprint","IMPRINT",FACE,{"disambiguationData":[TD([[makeQuery(id+"F0.imprint","IMPRINT",EDGE,{"derivedFrom":sQuery(id+"F0.wireOp",EDGE,"E201")}),1.0]])]});
            var Q39;
            {var subQ2=sQuery(id+"F0.wireOp",EDGE,"E196");Q39=makeQuery(id+"F0.imprint","IMPRINT",FACE,{"disambiguationData":[TD([[makeQuery(id+"F0.imprint","IMPRINT",EDGE,{"derivedFrom":subQ2}),1.0]])]});}
            var Q40;
            Q40=makeQuery(id+"F0.imprint","IMPRINT",FACE,{"disambiguationData":[TD([[makeQuery(id+"F0.imprint","IMPRINT",EDGE,{"derivedFrom":sQuery(id+"F0.wireOp",EDGE,"E211")}),1.0]])]});
            var Q41;
            Q41=makeQuery(id+"F0.imprint","IMPRINT",FACE,{"disambiguationData":[TD([[makeQuery(id+"F0.imprint","IMPRINT",EDGE,{"derivedFrom":sQuery(id+"F0.wireOp",EDGE,"E210")}),1.0]])]});
            var Q42;
            Q42=makeQuery(id+"F0.imprint","IMPRINT",FACE,{"disambiguationData":[TD([[makeQuery(id+"F0.imprint","IMPRINT",EDGE,{"derivedFrom":sQuery(id+"F0.wireOp",EDGE,"E191")}),1.0]])]});
            var Q43;
            Q43=makeQuery(id+"F0.imprint","IMPRINT",FACE,{"disambiguationData":[TD([[makeQuery(id+"F0.imprint","IMPRINT",EDGE,{"derivedFrom":sQuery(id+"F0.wireOp",EDGE,"E186")}),1.0]])]});
            var Q44;
            Q44=makeQuery(id+"F0.imprint","IMPRINT",FACE,{"disambiguationData":[TD([[makeQuery(id+"F0.imprint","IMPRINT",EDGE,{"derivedFrom":sQuery(id+"F0.wireOp",EDGE,"E212")}),1.0]])]});
            var Q45;
            Q45=makeQuery(id+"F0.imprint","IMPRINT",FACE,{"disambiguationData":[TD([[makeQuery(id+"F0.imprint","IMPRINT",EDGE,{"derivedFrom":sQuery(id+"F0.wireOp",EDGE,"E207")}),1.0]])]});
            var Q46;
            Q46=makeQuery(id+"F0.imprint","IMPRINT",FACE,{"disambiguationData":[TD([[makeQuery(id+"F0.imprint","IMPRINT",EDGE,{"derivedFrom":sQuery(id+"F0.wireOp",EDGE,"E208")}),1.0]])]});
            extrude(context, id + "F2", {"entities" : qUnion([Q0, Q1, Q2, Q3, Q4, Q5, Q6, Q7, Q8, Q9, Q10, Q11, Q12, Q13, Q14, Q15, Q16, Q17, Q18, Q19, Q20, Q21, Q22, Q23, Q24, Q25, Q26, Q27, Q28, Q29, Q30, Q31, Q32, Q33, Q34, Q35, Q36, Q37, Q38, Q39, Q40, Q41, Q42, Q43, Q44, Q45, Q46]), "operationType" : NewBodyOperationType.ADD, "depth" : 7 * mm, "offsetDistance" : 25.4 * mm});
        }
    });
